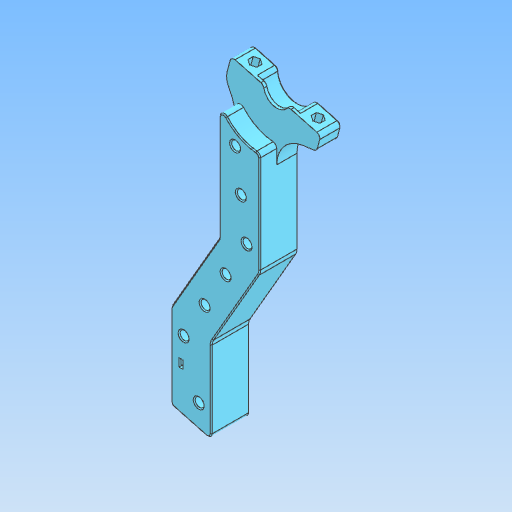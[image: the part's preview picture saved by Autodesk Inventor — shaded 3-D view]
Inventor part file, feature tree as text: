
AUTODESK INVENTOR PART (.ipt)
format: ipt  version: 2021.2 (Build 252289000, 289)  size: 444,416 bytes
history: native  units: mm
features: other x6, fillet x1, chamfer x1
ambient origin geometry x8: Origin, YZ Plane, XZ Plane, XY Plane, X Axis, Y Axis, Z Axis, Center Point
bodies: Body1 (feature_tree)
feature tree (8):
  other  "Твёрдое тело.ipt"
  other  "Непосредственное редактирование1"
  fillet  "Сопряжение1"  Radius=10.0mm
  chamfer  "Фаска1"  [1 undecoded]
  other  "Ножка левая верх::Твёрдое тело.ipt"
  other  "Элемент создания тегов1"
  other  "Твердое тело1"
  other  "Перенос1"
note: 1 required parameter value undecoded (feature->parameter linkage not recoverable at this tier; creation-order binding heuristic only, values carry confidence <= 0.55)
